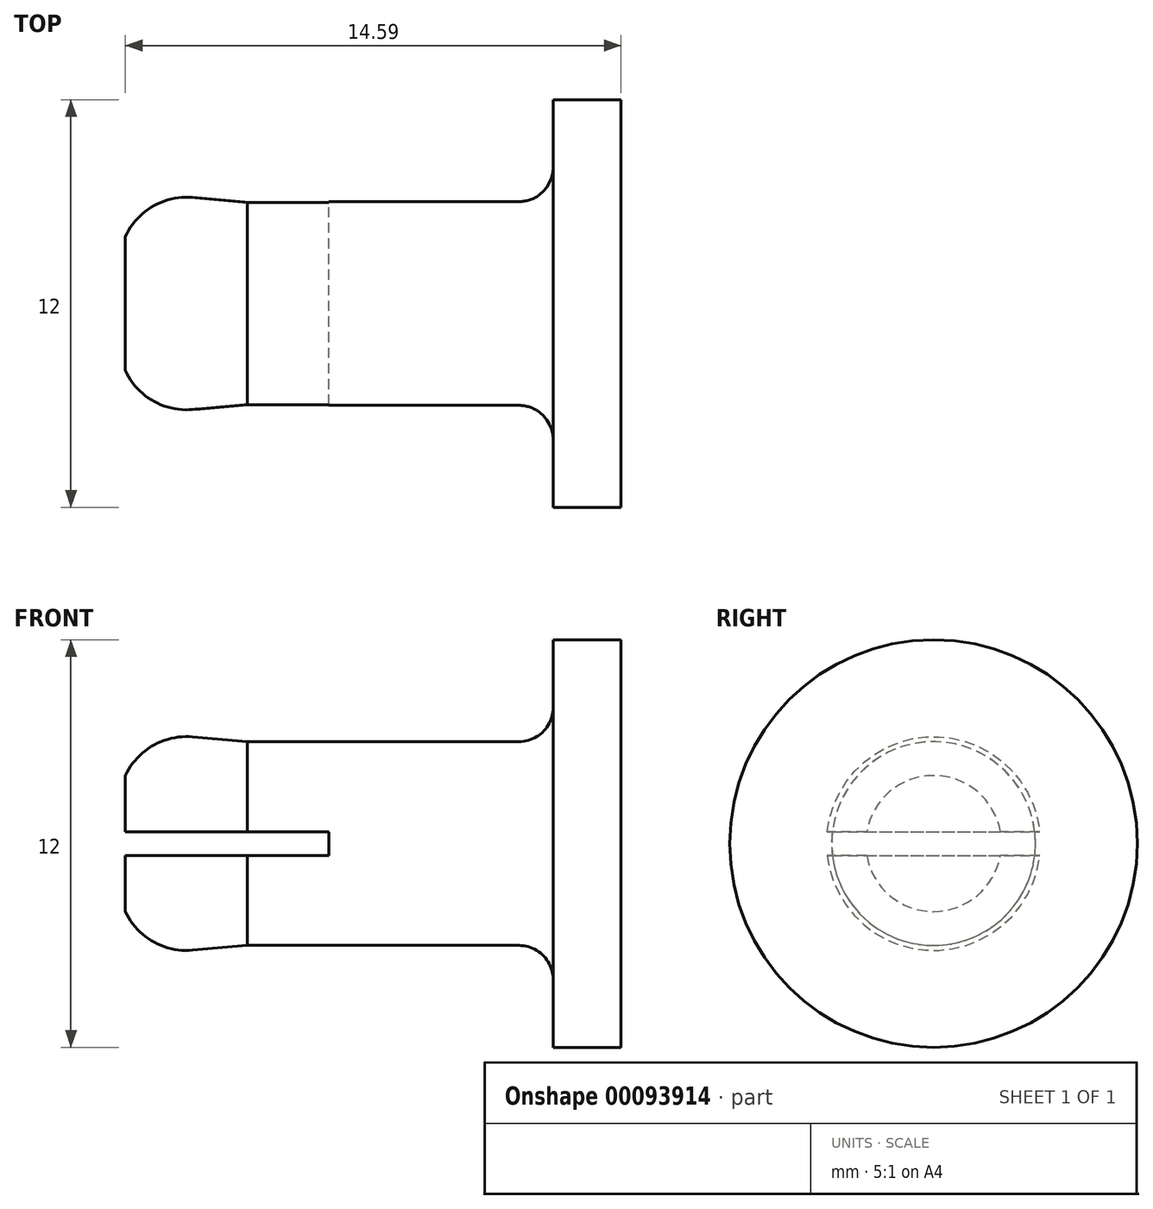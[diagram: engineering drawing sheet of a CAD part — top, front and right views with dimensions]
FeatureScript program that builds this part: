
annotation { "Feature Type Name" : "Feature", "Feature Type Description" : "" }
export const myFeature = defineFeature(function(context is Context, id is Id, definition is map)
    precondition{}
    {
        {
            var Q0;
            Q0=qCreatedBy(makeId("Front.planeOp"),FACE);
            var sketch = newSketch(context, id + "F0", { "sketchPlane" : qUnion([Q0])});
            skLineSegment(sketch, "E0", {"start": v(0, 0) * mm, "end": v(0, 6) * mm});
            skLineSegment(sketch, "E1", {"start": v(0, 6) * mm, "end": v(-2, 6) * mm});
            skLineSegment(sketch, "E2", {"start": v(-2, 6) * mm, "end": v(-2, 3) * mm});
            skLineSegment(sketch, "E3", {"start": v(-2, 3) * mm, "end": v(-11, 3) * mm});
            skLineSegment(sketch, "E4", {"start": v(-11, 3) * mm, "end": v(-12.61, 3.14) * mm});
            skLineSegment(sketch, "E5", {"start": v(-14.6, 2) * mm, "end": v(-14.6, 2) * mm});
            skLineSegment(sketch, "E6", {"start": v(-14.6, 2) * mm, "end": v(-14.6, 0) * mm});
            skLineSegment(sketch, "E7", {"start": v(-14.6, 0) * mm, "end": v(0, 0) * mm});
            skPoint(sketch, "E8.visualSharp", {"position": v(-14, 3.26) * mm});
            skArc(sketch, "E8.filletArc", {"start": v(-12.61, 3.14) * mm, "mid": v(-13.78, 2.88) * mm, "end": v(-14.6, 2) * mm});
            skSolve(sketch);
        }
        {
            var Q0;
            Q0=makeQuery(id+"F0.imprint","IMPRINT",FACE,{"disambiguationData":[TD([[makeQuery(id+"F0.imprint","IMPRINT",EDGE,{"derivedFrom":sQuery(id+"F0.wireOp",EDGE,"E0")}),1.0]])]});
            var Q1;
            Q1=sQuery(id+"F0.wireOp",EDGE,"E7");
            revolve(context, id + "F1", {"entities" : qUnion([Q0]), "axis" : qUnion([Q1]), "revolveType" : RevolveType.FULL});
        }
        {
            var Q0;
            Q0=makeQuery(id+"F1.opRevolve","SWEPT_FACE",FACE,{"disambiguationData":[OSD([sQuery(id+"F0.wireOp",EDGE,"E6")])]});
            var sketch = newSketch(context, id + "F2", { "sketchPlane" : qUnion([Q0])});
            skLineSegment(sketch, "E9.bottom", {"start": v(4, 0.35) * mm, "end": v(-4, 0.35) * mm});
            skLineSegment(sketch, "E9.top", {"start": v(4, -0.35) * mm, "end": v(-4, -0.35) * mm});
            skLineSegment(sketch, "E9.left", {"start": v(4, 0.35) * mm, "end": v(4, -0.35) * mm});
            skLineSegment(sketch, "E9.right", {"start": v(-4, 0.35) * mm, "end": v(-4, -0.35) * mm});
            skPoint(sketch, "E9.middle", {"position": v(0, 0) * mm});
            skLineSegment(sketch, "E10.bottom", {"start": v(-4, 0.35) * mm, "end": v(4, 0.35) * mm});
            skLineSegment(sketch, "E10.top", {"start": v(-4, -4.18) * mm, "end": v(4, -4.18) * mm});
            skLineSegment(sketch, "E10.left", {"start": v(-4, 0.35) * mm, "end": v(-4, -4.18) * mm});
            skLineSegment(sketch, "E10.right", {"start": v(4, 0.35) * mm, "end": v(4, -4.18) * mm});
            skArc(sketch, "E11", {"start": v(-2.98, -0.35) * mm, "mid": v(0, -3) * mm, "end": v(2.98, -0.35) * mm});
            skLineSegment(sketch, "E12", {"start": v(-0.25, 0.35) * mm, "end": v(-0.25, 4.35) * mm});
            skLineSegment(sketch, "E13", {"start": v(-0.25, 4.35) * mm, "end": v(0.25, 4.35) * mm});
            skLineSegment(sketch, "E14", {"start": v(0.25, 4.35) * mm, "end": v(0.25, 0.35) * mm});
            skPoint(sketch, "E15", {"position": v(0, 4.35) * mm});
            skLineSegment(sketch, "E16", {"start": v(-0.25, 0.35) * mm, "end": v(-0.25, 0) * mm});
            skLineSegment(sketch, "E17", {"start": v(0.25, 0) * mm, "end": v(0.25, 0.35) * mm});
            skLineSegment(sketch, "E18", {"start": v(-0.25, 0) * mm, "end": v(-0.25, -0.35) * mm});
            skLineSegment(sketch, "E19", {"start": v(0.25, 0) * mm, "end": v(0.25, -0.35) * mm});
            skSolve(sketch);
        }
        {
            var Q0;
            {var subQ0=sQuery(id+"F2.wireOp",EDGE,"E10.left");var subQ1=sQuery(id+"F2.wireOp",EDGE,"E9.top");var subQ2=makeQuery(id+"F2.imprint","INTERSECT",VERTEX,{"derivedFrom":[subQ1,subQ0]});Q0=makeQuery(id+"F2.imprint","IMPRINT",FACE,{"disambiguationData":[TD([[makeQuery(id+"F2.imprint","IMPRINT",EDGE,{"disambiguationData":[TD([[subQ2,1.0]])],"derivedFrom":subQ1}),-1.0]])]});}
            var Q1;
            {var subQ0=sQuery(id+"F2.wireOp",EDGE,"E9.top");var subQ1=sQuery(id+"F0.wireOp",EDGE,"E6");var subQ2=makeQuery(id+"F1.opRevolve","SWEPT_EDGE",EDGE,{"disambiguationData":[OSD([subQ1,sQuery(id+"F0.wireOp",EDGE,"7DEYfaqh-BLmM-Zio8-RinN-fUETocERDkPJ")])]});var subQ3=makeQuery(id+"F2.imprint","INTERSECT",VERTEX,{"disambiguationData":[OD(1.0)],"derivedFrom":[subQ2,subQ0]});Q1=makeQuery(id+"F2.imprint","IMPRINT",FACE,{"disambiguationData":[TD([[makeQuery(id+"F2.imprint","IMPRINT",EDGE,{"disambiguationData":[TD([[subQ3,-1.0]])],"derivedFrom":subQ0}),-1.0]])]});}
            var Q2;
            {var subQ1=sQuery(id+"F2.wireOp",EDGE,"E16");Q2=makeQuery(id+"F2.imprint","IMPRINT",FACE,{"disambiguationData":[TD([[makeQuery(id+"F2.imprint","IMPRINT",EDGE,{"derivedFrom":subQ1}),-1.0]])]});}
            var Q3;
            {var subQ0=sQuery(id+"F2.wireOp",EDGE,"E16");Q3=makeQuery(id+"F2.imprint","IMPRINT",FACE,{"disambiguationData":[TD([[makeQuery(id+"F2.imprint","IMPRINT",EDGE,{"derivedFrom":subQ0}),1.0]])]});}
            var Q4;
            {var subQ0=sQuery(id+"F2.wireOp",EDGE,"E10.right");var subQ1=sQuery(id+"F2.wireOp",EDGE,"E9.top");var subQ2=makeQuery(id+"F2.imprint","INTERSECT",VERTEX,{"derivedFrom":[subQ1,subQ0]});Q4=makeQuery(id+"F2.imprint","IMPRINT",FACE,{"disambiguationData":[TD([[makeQuery(id+"F2.imprint","IMPRINT",EDGE,{"disambiguationData":[TD([[subQ2,-1.0]])],"derivedFrom":subQ1}),-1.0]])]});}
            var Q5;
            {var subQ0=sQuery(id+"F2.wireOp",EDGE,"E9.top");var subQ1=sQuery(id+"F0.wireOp",EDGE,"E6");var subQ2=makeQuery(id+"F1.opRevolve","SWEPT_EDGE",EDGE,{"disambiguationData":[OSD([sQuery(id+"F0.wireOp",EDGE,"E5"),subQ1])]});var subQ3=makeQuery(id+"F2.imprint","INTERSECT",VERTEX,{"disambiguationData":[OD(0.0)],"derivedFrom":[subQ2,subQ0]});Q5=makeQuery(id+"F2.imprint","IMPRINT",FACE,{"disambiguationData":[TD([[makeQuery(id+"F2.imprint","IMPRINT",EDGE,{"disambiguationData":[TD([[subQ3,-1.0]])],"derivedFrom":subQ0}),-1.0]])]});}
            var Q6;
            {var subQ0=sQuery(id+"F2.wireOp",EDGE,"E17");Q6=makeQuery(id+"F2.imprint","IMPRINT",FACE,{"disambiguationData":[TD([[makeQuery(id+"F2.imprint","IMPRINT",EDGE,{"derivedFrom":subQ0}),-1.0]])]});}
            extrude(context, id + "F3", {"entities" : qUnion([Q0, Q1, Q2, Q3, Q4, Q5, Q6]), "operationType" : NewBodyOperationType.REMOVE, "oppositeDirection" : true, "depth" : 6 * mm});
        }
        {
            var Q0;
            Q0=makeQuery(id+"F1.opRevolve","SWEPT_EDGE",EDGE,{"disambiguationData":[OSD([sQuery(id+"F0.wireOp",EDGE,"E2"),sQuery(id+"F0.wireOp",EDGE,"E3")])]});
            fillet(context, id + "F4", {"entities" : qUnion([Q0]), "radius" : 1 * mm, "tangentPropagation" : true, "allowEdgeOverflow" : false});
        }
    });
